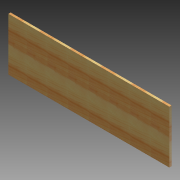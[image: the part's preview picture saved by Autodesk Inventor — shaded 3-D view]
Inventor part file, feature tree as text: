
AUTODESK INVENTOR PART (.ipt)
format: ipt  version: 2012 (Build 160160000, 160)  size: 84,992 bytes
history: native  units: in
note: dims shown in document units (in); Inventor stores cm internally (conversion verified against a paired STEP export)
features: extrude x1, sketch x1
ambient origin geometry x8: Origin, YZ Plane, XZ Plane, XY Plane, X Axis, Y Axis, Z Axis, Center Point
bodies: Solid1 (feature_tree)
feature tree (2):
  extrude  "Extrusion1"  Depth=9.0in
  sketch  "Sketch1"  dims[d0=27.5in d1=9.0in d2=0.375in d3=0.0in]
